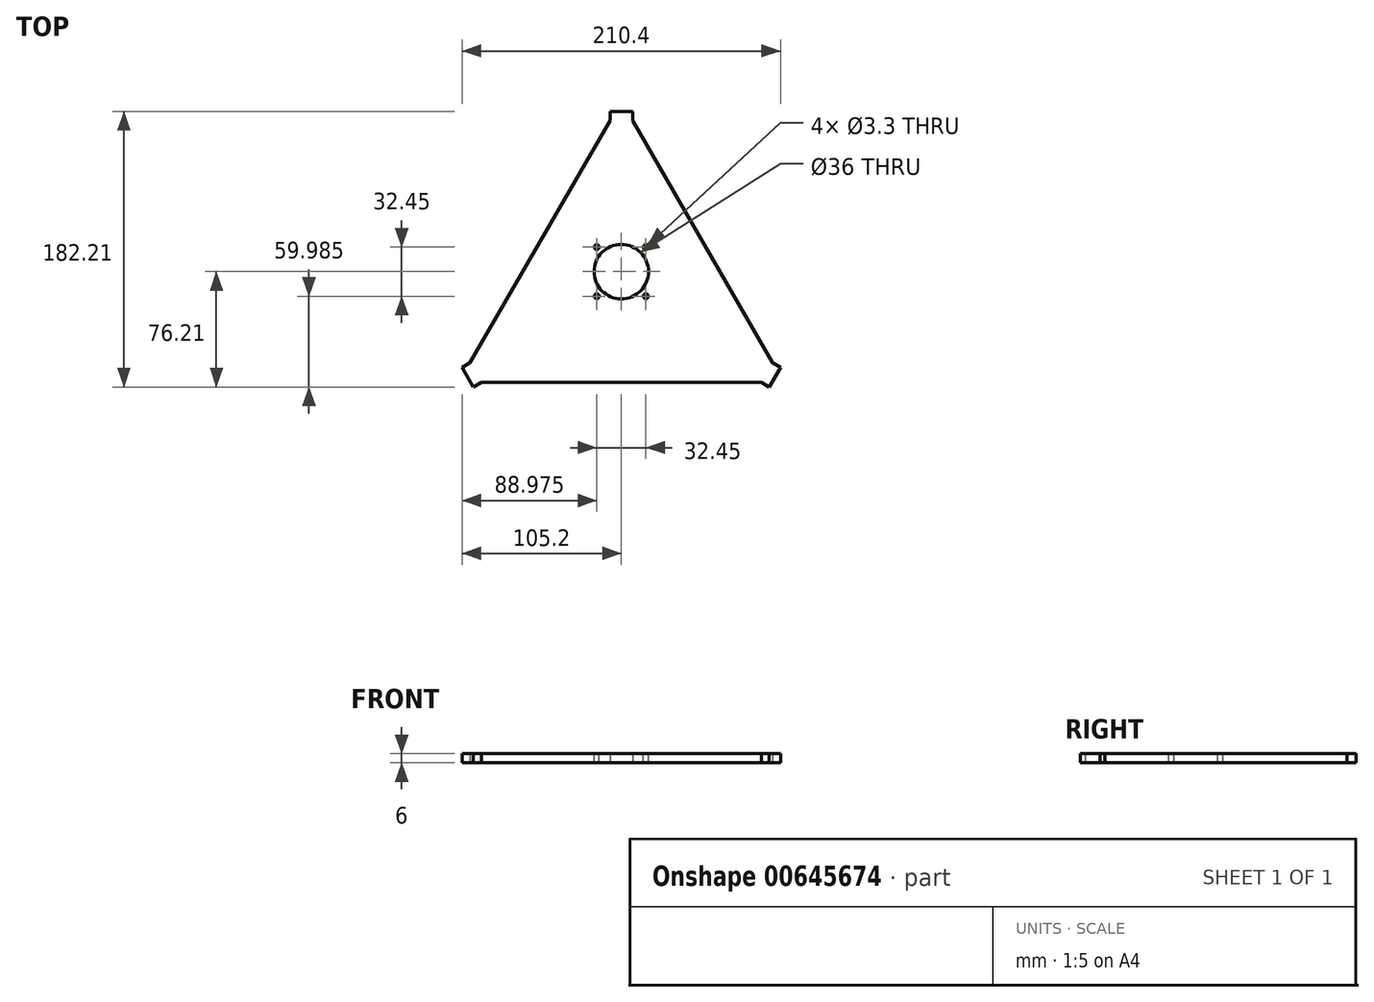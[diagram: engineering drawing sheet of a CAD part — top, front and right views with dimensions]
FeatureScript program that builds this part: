
annotation { "Feature Type Name" : "Feature", "Feature Type Description" : "" }
export const myFeature = defineFeature(function(context is Context, id is Id, definition is map)
    precondition{}
    {
        {
            var Q0;
            Q0=qCreatedBy(makeId("Top.planeOp"),FACE);
            var sketch = newSketch(context, id + "F0", { "sketchPlane" : qUnion([Q0])});
            skLineSegment(sketch, "E0", {"start": v(0, 0) * mm, "end": v(0, 150) * mm});
            skLineSegment(sketch, "E1", {"start": v(0, 0) * mm, "end": v(-129.9, -75) * mm});
            skLineSegment(sketch, "E2", {"start": v(0, 0) * mm, "end": v(129.9, -75) * mm});
            skLineSegment(sketch, "E3.bottom", {"start": v(7.5, 117.14) * mm, "end": v(-7.5, 117.14) * mm});
            skLineSegment(sketch, "E3.top", {"start": v(7.5, 111.14) * mm, "end": v(-7.5, 111.14) * mm});
            skLineSegment(sketch, "E3.left", {"start": v(7.5, 117.14) * mm, "end": v(7.5, 111.14) * mm});
            skLineSegment(sketch, "E3.right", {"start": v(-7.5, 117.14) * mm, "end": v(-7.5, 111.14) * mm});
            skPoint(sketch, "E3.middle", {"position": v(0, 114.14) * mm});
            skLineSegment(sketch, "E4.bottom", {"start": v(-105.2, -52.07) * mm, "end": v(-100, -49.07) * mm});
            skLineSegment(sketch, "E4.top", {"start": v(-97.7, -65.07) * mm, "end": v(-92.5, -62.07) * mm});
            skLineSegment(sketch, "E4.left", {"start": v(-105.2, -52.07) * mm, "end": v(-97.7, -65.07) * mm});
            skLineSegment(sketch, "E4.right", {"start": v(-100, -49.07) * mm, "end": v(-92.5, -62.07) * mm});
            skPoint(sketch, "E4.middle", {"position": v(-98.85, -57.07) * mm});
            skLineSegment(sketch, "E5.bottom", {"start": v(105.2, -52.07) * mm, "end": v(100, -49.07) * mm});
            skLineSegment(sketch, "E5.top", {"start": v(97.7, -65.07) * mm, "end": v(92.5, -62.07) * mm});
            skLineSegment(sketch, "E5.left", {"start": v(105.2, -52.07) * mm, "end": v(97.7, -65.07) * mm});
            skLineSegment(sketch, "E5.right", {"start": v(100, -49.07) * mm, "end": v(92.5, -62.07) * mm});
            skPoint(sketch, "E5.middle", {"position": v(98.85, -57.07) * mm});
            skLineSegment(sketch, "E6", {"start": v(-7.5, 111.14) * mm, "end": v(-100, -49.07) * mm});
            skLineSegment(sketch, "E7", {"start": v(-92.5, -62.07) * mm, "end": v(92.5, -62.07) * mm});
            skLineSegment(sketch, "E8", {"start": v(100, -49.07) * mm, "end": v(7.5, 111.14) * mm});
            skSolve(sketch);
        }
        {
            var Q0;
            {var subQ0=sQuery(id+"F0.wireOp",EDGE,"E8");Q0=makeQuery(id+"F0.imprint","IMPRINT",FACE,{"disambiguationData":[TD([[makeQuery(id+"F0.imprint","IMPRINT",EDGE,{"derivedFrom":subQ0}),1.0]])]});}
            var Q1;
            {var subQ0=sQuery(id+"F0.wireOp",EDGE,"E6");Q1=makeQuery(id+"F0.imprint","IMPRINT",FACE,{"disambiguationData":[TD([[makeQuery(id+"F0.imprint","IMPRINT",EDGE,{"derivedFrom":subQ0}),1.0]])]});}
            var Q2;
            {var subQ5=sQuery(id+"F0.wireOp",EDGE,"E3.left");Q2=makeQuery(id+"F0.imprint","IMPRINT",FACE,{"disambiguationData":[TD([[makeQuery(id+"F0.imprint","IMPRINT",EDGE,{"derivedFrom":subQ5}),-1.0]])]});}
            var Q3;
            {var subQ5=sQuery(id+"F0.wireOp",EDGE,"E3.right");Q3=makeQuery(id+"F0.imprint","IMPRINT",FACE,{"disambiguationData":[TD([[makeQuery(id+"F0.imprint","IMPRINT",EDGE,{"derivedFrom":subQ5}),1.0]])]});}
            var Q4;
            {var subQ0=sQuery(id+"F0.wireOp",EDGE,"E7");Q4=makeQuery(id+"F0.imprint","IMPRINT",FACE,{"disambiguationData":[TD([[makeQuery(id+"F0.imprint","IMPRINT",EDGE,{"derivedFrom":subQ0}),1.0]])]});}
            var Q5;
            {var subQ5=sQuery(id+"F0.wireOp",EDGE,"E4.bottom");Q5=makeQuery(id+"F0.imprint","IMPRINT",FACE,{"disambiguationData":[TD([[makeQuery(id+"F0.imprint","IMPRINT",EDGE,{"derivedFrom":subQ5}),-1.0]])]});}
            var Q6;
            {var subQ5=sQuery(id+"F0.wireOp",EDGE,"E4.top");Q6=makeQuery(id+"F0.imprint","IMPRINT",FACE,{"disambiguationData":[TD([[makeQuery(id+"F0.imprint","IMPRINT",EDGE,{"derivedFrom":subQ5}),1.0]])]});}
            var Q7;
            {var subQ5=sQuery(id+"F0.wireOp",EDGE,"E5.bottom");Q7=makeQuery(id+"F0.imprint","IMPRINT",FACE,{"disambiguationData":[TD([[makeQuery(id+"F0.imprint","IMPRINT",EDGE,{"derivedFrom":subQ5}),1.0]])]});}
            var Q8;
            {var subQ5=sQuery(id+"F0.wireOp",EDGE,"E5.top");Q8=makeQuery(id+"F0.imprint","IMPRINT",FACE,{"disambiguationData":[TD([[makeQuery(id+"F0.imprint","IMPRINT",EDGE,{"derivedFrom":subQ5}),-1.0]])]});}
            extrude(context, id + "F1", {"entities" : qUnion([Q0, Q1, Q2, Q3, Q4, Q5, Q6, Q7, Q8]), "depth" : 6 * mm, "offsetDistance" : 25 * mm});
        }
        {
            var Q0;
            Q0=makeQuery(id+"F1.opExtrude","CAP_FACE",FACE,{"disambiguationData":[OSD([sQuery(id+"F0.wireOp",EDGE,"E3.bottom"),sQuery(id+"F0.wireOp",EDGE,"E3.left"),sQuery(id+"F0.wireOp",EDGE,"E3.right"),sQuery(id+"F0.wireOp",EDGE,"E4.bottom"),sQuery(id+"F0.wireOp",EDGE,"E4.top"),sQuery(id+"F0.wireOp",EDGE,"E4.left"),sQuery(id+"F0.wireOp",EDGE,"E5.bottom"),sQuery(id+"F0.wireOp",EDGE,"E5.top"),sQuery(id+"F0.wireOp",EDGE,"E5.left"),sQuery(id+"F0.wireOp",EDGE,"E6"),sQuery(id+"F0.wireOp",EDGE,"E7"),sQuery(id+"F0.wireOp",EDGE,"E8")])],"isStart":false});
            var sketch = newSketch(context, id + "F2", { "sketchPlane" : qUnion([Q0])});
            skCircle(sketch, "E9", {"center": v(0, 11.14) * mm, "radius": 18 * mm});
            skLineSegment(sketch, "E10.bottom", {"start": v(19.88, 31.01) * mm, "end": v(-19.88, 31.01) * mm});
            skLineSegment(sketch, "E10.top", {"start": v(19.88, -8.74) * mm, "end": v(-19.88, -8.74) * mm});
            skLineSegment(sketch, "E10.left", {"start": v(19.88, 31.01) * mm, "end": v(19.88, -8.74) * mm});
            skLineSegment(sketch, "E10.right", {"start": v(-19.88, 31.01) * mm, "end": v(-19.88, -8.74) * mm});
            skCircle(sketch, "E11", {"center": v(-16.23, 27.36) * mm, "radius": 1.65 * mm});
            skCircle(sketch, "E12", {"center": v(16.23, 27.36) * mm, "radius": 1.65 * mm});
            skCircle(sketch, "E13", {"center": v(16.23, -5.09) * mm, "radius": 1.65 * mm});
            skCircle(sketch, "E14", {"center": v(-16.23, -5.09) * mm, "radius": 1.65 * mm});
            skSolve(sketch);
        }
        {
            var Q0;
            Q0=makeQuery(id+"F2.imprint","IMPRINT",FACE,{"disambiguationData":[TD([[makeQuery(id+"F2.imprint","IMPRINT",EDGE,{"derivedFrom":sQuery(id+"F2.wireOp",EDGE,"E9")}),1.0]])]});
            var Q1;
            Q1=makeQuery(id+"F2.imprint","IMPRINT",FACE,{"disambiguationData":[TD([[makeQuery(id+"F2.imprint","IMPRINT",EDGE,{"derivedFrom":sQuery(id+"F2.wireOp",EDGE,"E11")}),1.0]])]});
            var Q2;
            Q2=makeQuery(id+"F2.imprint","IMPRINT",FACE,{"disambiguationData":[TD([[makeQuery(id+"F2.imprint","IMPRINT",EDGE,{"derivedFrom":sQuery(id+"F2.wireOp",EDGE,"E12")}),1.0]])]});
            var Q3;
            Q3=makeQuery(id+"F2.imprint","IMPRINT",FACE,{"disambiguationData":[TD([[makeQuery(id+"F2.imprint","IMPRINT",EDGE,{"derivedFrom":sQuery(id+"F2.wireOp",EDGE,"E13")}),1.0]])]});
            var Q4;
            Q4=makeQuery(id+"F2.imprint","IMPRINT",FACE,{"disambiguationData":[TD([[makeQuery(id+"F2.imprint","IMPRINT",EDGE,{"derivedFrom":sQuery(id+"F2.wireOp",EDGE,"E14")}),1.0]])]});
            extrude(context, id + "F3", {"entities" : qUnion([Q0, Q1, Q2, Q3, Q4]), "operationType" : NewBodyOperationType.REMOVE, "endBound" : BoundingType.THROUGH_ALL, "oppositeDirection" : true, "depth" : 25 * mm, "offsetDistance" : 25 * mm});
        }
    });
